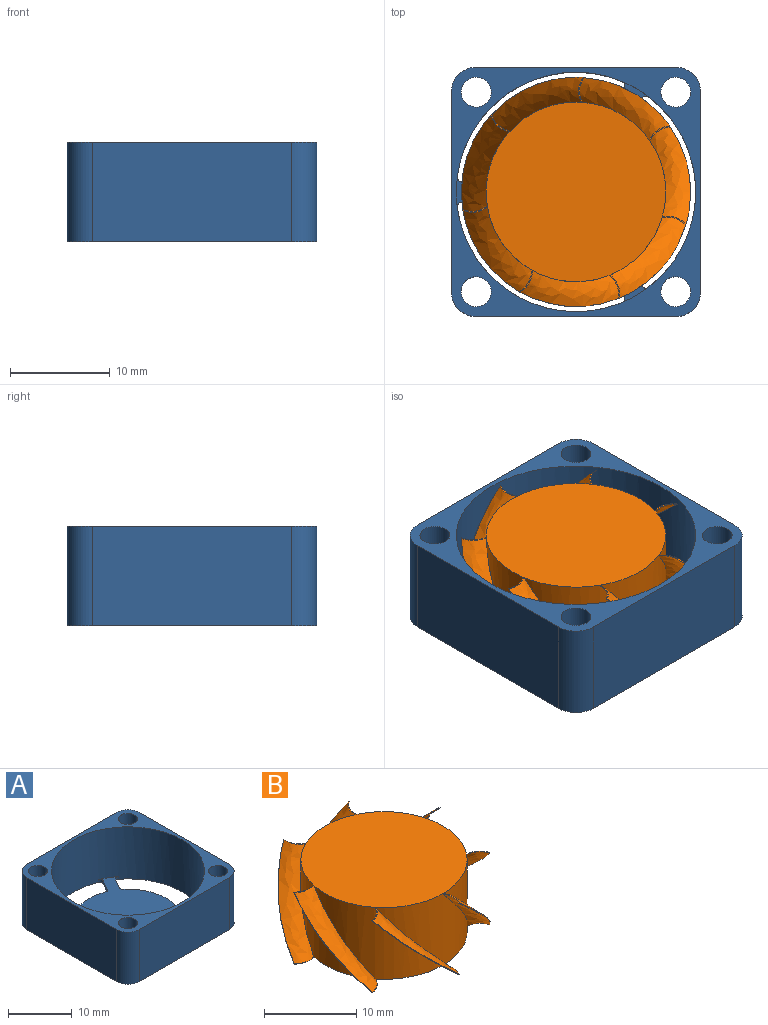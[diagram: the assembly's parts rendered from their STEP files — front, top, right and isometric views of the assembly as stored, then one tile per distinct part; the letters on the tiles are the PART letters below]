
ASSEMBLY  parts=2 mates=2
PART A: 37 faces, bbox 25x25x10 mm
  f0: plane 20x10mm, normal (-1,0,0), area 200mm2, adj f1,f10,f13,f14
  f1: cylinder r=2.5mm len=10mm, axis (0,0,-1), area 39.3mm2, adj f0,f2,f13,f14
  f2: plane 20x10mm, normal (0,-1,0), area 200mm2, adj f1,f3,f13,f14
  f3: cylinder r=2.5mm len=10mm, axis (0,0,-1), area 39.3mm2, adj f2,f4,f13,f14
  f4: plane 20x10mm, normal (1,0,0), area 200mm2, adj f3,f5,f13,f14
  f5: cylinder r=2.5mm len=10mm, axis (0,0,-1), area 39.3mm2, adj f4,f6,f13,f14
  f6: plane 20x10mm, normal (0,1,0), area 200mm2, adj f5,f10,f13,f14
  f7: cylinder r=1.5mm len=10mm, axis (0,0,-1), area 94.2mm2, adj f13,f14
  f8: cylinder r=1.5mm len=10mm, axis (0,0,-1), area 94.2mm2, adj f13,f14
  f9: cylinder r=12mm len=24mm, axis (0,0,-1), area 749.3mm2, adj f13,f14,f24,f31,f32,f33,f34,f35
  f10: cylinder r=2.5mm len=10mm, axis (0,0,-1), area 39.3mm2, adj f0,f6,f13,f14
  f11: cylinder r=1.5mm len=10mm, axis (0,0,-1), area 94.2mm2, adj f13,f14
  f12: cylinder r=1.5mm len=10mm, axis (0,0,-1), area 94.2mm2, adj f13,f14
  f13: plane 25x25mm, normal (0,0,1), area 139mm2, adj f0,f1,f2,f3,f4,f5,f6,f7
  f14: plane 25x25mm, normal (0,0,-1), area 387.6mm2, adj f0,f1,f2,f3,f4,f5,f6,f7
  f15: cylinder r=8.5mm len=11.35mm, axis (0,0,-1), area 7.5mm2, adj f14,f24,f25,f26
  f16: plane 2.19x1.26mm, normal (-0.87,0.5,0), area 1.3mm2, adj f14,f24,f26,f31
  f17: plane 2.19x1.26mm, normal (0.87,-0.5,0), area 1.3mm2, adj f14,f24,f27,f32
  f18: cylinder r=8.5mm len=13.1mm, axis (0,0,-1), area 7.5mm2, adj f14,f24,f27,f28
  f19: plane 2.19x1.26mm, normal (0.87,0.5,0), area 1.3mm2, adj f14,f24,f28,f33
  f20: plane 2.19x1.26mm, normal (-0.87,-0.5,0), area 1.3mm2, adj f14,f24,f29,f34
  f21: cylinder r=8.5mm len=11.35mm, axis (0,0,-1), area 7.5mm2, adj f14,f24,f29,f30
  f22: plane 2.53x0.5mm, normal (0,-1,0), area 1.3mm2, adj f14,f24,f30,f35
  f23: plane 2.53x0.5mm, normal (0,1,0), area 1.3mm2, adj f14,f24,f25,f36
  f24: plane 22.17x20.5mm, normal (0,0,1), area 248.7mm2, adj f9,f15,f16,f17,f18,f19,f20,f21
  f25: cylinder r=0.5mm len=0.5mm, axis (0,0,-1), area 0.4mm2, adj f14,f15,f23,f24
  f26: cylinder r=0.5mm len=0.61mm, axis (0,0,-1), area 0.4mm2, adj f14,f15,f16,f24
  f27: cylinder r=0.5mm len=0.64mm, axis (0,0,-1), area 0.4mm2, adj f14,f17,f18,f24
  f28: cylinder r=0.5mm len=0.64mm, axis (0,0,-1), area 0.4mm2, adj f14,f18,f19,f24
  f29: cylinder r=0.5mm len=0.61mm, axis (0,0,-1), area 0.4mm2, adj f14,f20,f21,f24
  f30: cylinder r=0.5mm len=0.5mm, axis (0,0,-1), area 0.4mm2, adj f14,f21,f22,f24
  f31: cylinder r=0.5mm len=0.71mm, axis (0,0,-1), area 0.4mm2, adj f9,f14,f16,f24
  f32: cylinder r=0.5mm len=0.74mm, axis (0,0,-1), area 0.4mm2, adj f9,f14,f17,f24
  f33: cylinder r=0.5mm len=0.74mm, axis (0,0,-1), area 0.4mm2, adj f9,f14,f19,f24
  f34: cylinder r=0.5mm len=0.71mm, axis (0,0,-1), area 0.4mm2, adj f9,f14,f20,f24
  f35: cylinder r=0.5mm len=0.57mm, axis (0,0,-1), area 0.4mm2, adj f9,f14,f22,f24
  f36: cylinder r=0.5mm len=0.57mm, axis (0,0,-1), area 0.4mm2, adj f9,f14,f23,f24
PART B: 32 faces, bbox 23.6x23x14.3 mm
  f0: cylinder r=9mm len=10.96mm, axis (0,0,-1), area 75.8mm2, adj f7,f8,f26,f31
  f1: cylinder r=9mm len=13.66mm, axis (0,0,-1), area 75.8mm2, adj f7,f8,f23,f28
  f2: cylinder r=9mm len=12.63mm, axis (0,0,-1), area 75.8mm2, adj f7,f8,f20,f25
  f3: cylinder r=9mm len=12.62mm, axis (0,0,-1), area 75.8mm2, adj f7,f8,f17,f22
  f4: cylinder r=9mm len=13.66mm, axis (0,0,-1), area 75.8mm2, adj f7,f8,f14,f19
  f5: cylinder r=9mm len=10.95mm, axis (0,0,-1), area 75.8mm2, adj f7,f8,f11,f16
  f6: cylinder r=9mm len=14.01mm, axis (0,0,-1), area 75.8mm2, adj f7,f8,f13,f29
  f7: plane 22.43x21.86mm, normal (0,0,1), area 256.2mm2, adj f0,f1,f2,f3,f4,f5,f6,f11
  f8: plane 22.43x21.86mm, normal (0,0,-1), area 29.2mm2, adj f0,f1,f2,f3,f4,f5,f6,f9
  f9: cylinder r=8.5mm len=17mm, axis (0,0,-1), area 480.7mm2, adj f8,f10
  f10: plane 17x17mm, normal (0,0,-1), area 227mm2, adj f9
  f11: bspline ~14.25x11.68mm, area 34mm2, adj f5,f7,f8,f12
  f12: bspline ~14.25x11.26mm, area 1mm2, adj f7,f8,f11,f13
  f13: bspline ~14.25x11.76mm, area 34mm2, adj f6,f7,f8,f12
  f14: bspline ~14.33x14.25mm, area 34mm2, adj f4,f7,f8,f15
  f15: bspline ~14.41x14.25mm, area 1mm2, adj f7,f8,f14,f16
  f16: bspline ~14.33x14.25mm, area 34mm2, adj f5,f7,f8,f15
  f17: bspline ~14.25x11.24mm, area 34mm2, adj f3,f7,f8,f18
  f18: bspline ~14.25x11.26mm, area 1mm2, adj f7,f8,f17,f19
  f19: bspline ~14.25x11.16mm, area 34mm2, adj f4,f7,f8,f18
  f20: bspline ~14.25x14.08mm, area 34mm2, adj f2,f7,f8,f21
  f21: bspline ~14.25x14.04mm, area 1mm2, adj f7,f8,f20,f22
  f22: bspline ~14.25x14.11mm, area 34mm2, adj f3,f7,f8,f21
  f23: bspline ~14.25x12.94mm, area 34mm2, adj f1,f7,f8,f24
  f24: bspline ~14.25x12.98mm, area 1mm2, adj f7,f8,f23,f25
  f25: bspline ~14.25x12.88mm, area 34mm2, adj f2,f7,f8,f24
  f26: bspline ~14.25x13.21mm, area 34mm2, adj f0,f7,f8,f27
  f27: bspline ~14.25x12.98mm, area 1mm2, adj f7,f8,f26,f28
  f28: bspline ~14.25x13.26mm, area 34mm2, adj f1,f7,f8,f27
  f29: bspline ~14.25x13.98mm, area 34mm2, adj f6,f7,f8,f30
  f30: bspline ~14.25x14.04mm, area 1mm2, adj f7,f8,f29,f31
  f31: bspline ~14.25x13.95mm, area 34mm2, adj f0,f7,f8,f30
PLACE A t=(0.36,-0.6,-4.96)mm fixed
PLACE B rot(axis=(0,0,1),21.9deg) t=(0.36,-0.6,-4.46)mm
MATE planar B.f8 <-> A.f9  axis (0,0,-1) through (-4.12,-8.41,-4.46)mm
MATE cylindrical B.f0 <-> A.f9  axis (0,0,-1) through (0.36,-0.6,0.29)mm
